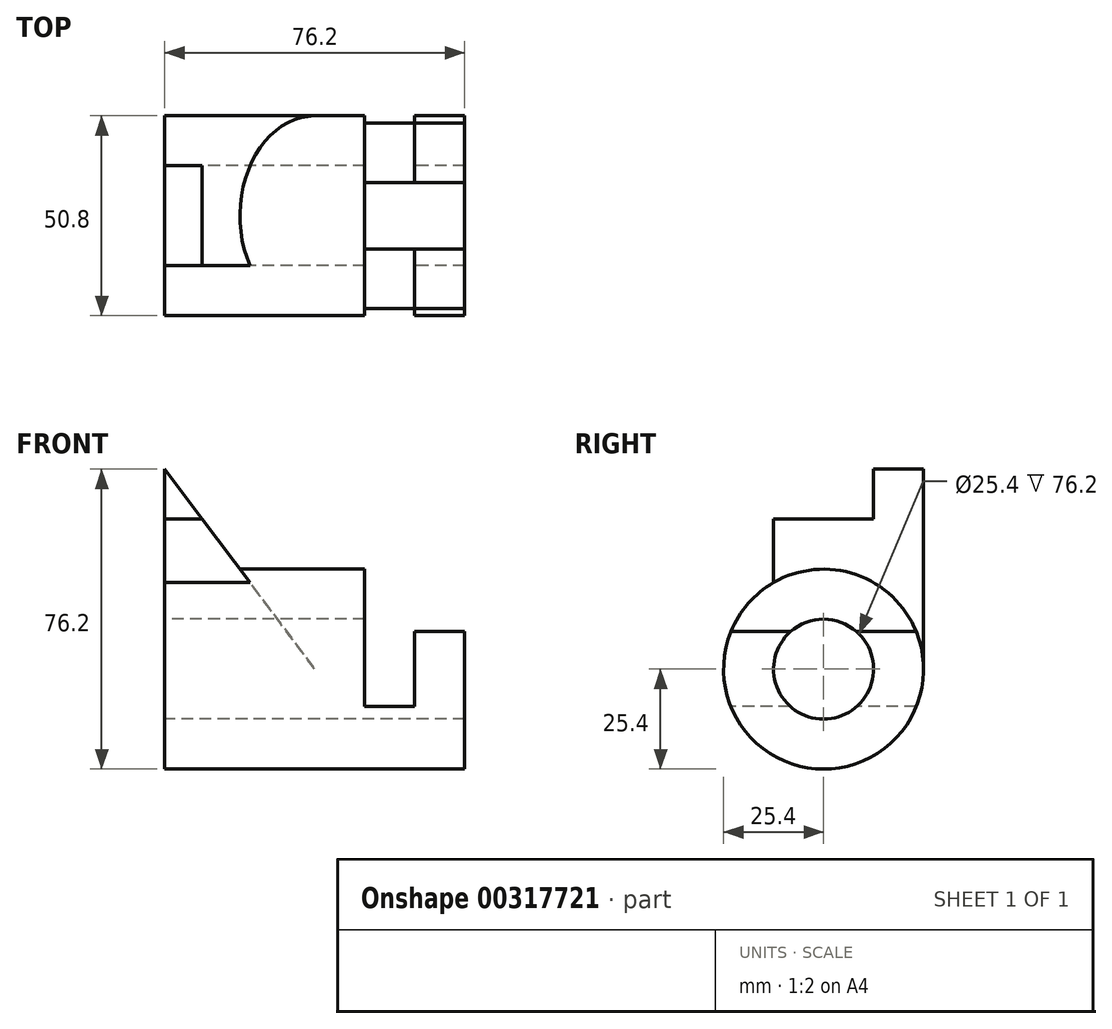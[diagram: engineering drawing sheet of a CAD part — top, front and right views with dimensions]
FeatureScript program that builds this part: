
annotation { "Feature Type Name" : "Feature", "Feature Type Description" : "" }
export const myFeature = defineFeature(function(context is Context, id is Id, definition is map)
    precondition{}
    {
        {
            var Q0;
            Q0=qCreatedBy(makeId("Right.planeOp"),FACE);
            var sketch = newSketch(context, id + "F0", { "sketchPlane" : qUnion([Q0])});
            skCircle(sketch, "E0", {"center": v(0, 0) * mm, "radius": 12.7 * mm});
            skCircle(sketch, "E1", {"center": v(0, 0) * mm, "radius": 25.4 * mm});
            skSolve(sketch);
        }
        {
            var Q0;
            Q0=makeQuery(id+"F0.imprint","IMPRINT",FACE,{"disambiguationData":[TD([[makeQuery(id+"F0.imprint","IMPRINT",EDGE,{"derivedFrom":sQuery(id+"F0.wireOp",EDGE,"E0")}),-1.0]])]});
            extrude(context, id + "F1", {"entities" : qUnion([Q0]), "depth" : 76.2 * mm});
        }
        {
            var Q0;
            Q0=qCreatedBy(makeId("Front.planeOp"),FACE);
            var sketch = newSketch(context, id + "F2", { "sketchPlane" : qUnion([Q0])});
            skLineSegment(sketch, "E2", {"start": v(50.8, 25.4) * mm, "end": v(50.8, -9.53) * mm});
            skLineSegment(sketch, "E3", {"start": v(50.8, -9.53) * mm, "end": v(63.5, -9.53) * mm});
            skLineSegment(sketch, "E4", {"start": v(63.5, -9.53) * mm, "end": v(63.5, 9.52) * mm});
            skLineSegment(sketch, "E5", {"start": v(63.5, 9.53) * mm, "end": v(76.2, 9.53) * mm});
            skLineSegment(sketch, "E6", {"start": v(76.2, 9.53) * mm, "end": v(76.2, 25.4) * mm});
            skLineSegment(sketch, "E7", {"start": v(76.2, 25.4) * mm, "end": v(50.8, 25.4) * mm});
            skLineSegment(sketch, "E8", {"start": v(0, 25.4) * mm, "end": v(76.2, 25.4) * mm});
            skSolve(sketch);
        }
        {
            var Q0;
            Q0 = qSketchRegion(id + "F2", true);
            extrude(context, id + "F3", {"entities" : qUnion([Q0]), "operationType" : NewBodyOperationType.REMOVE, "endBound" : BoundingType.SYMMETRIC, "oppositeDirection" : true, "depth" : 53.34 * mm});
        }
        {
            var Q0;
            Q0=qCreatedBy(makeId("Front.planeOp"),FACE);
            var sketch = newSketch(context, id + "F4", { "sketchPlane" : qUnion([Q0])});
            skLineSegment(sketch, "E9", {"start": v(0, 0) * mm, "end": v(0, 50.8) * mm});
            skLineSegment(sketch, "E10", {"start": v(0, 50.8) * mm, "end": v(38.1, 0) * mm});
            skLineSegment(sketch, "E11", {"start": v(38.1, 0) * mm, "end": v(0, 0) * mm});
            skSolve(sketch);
        }
        {
            var Q0;
            Q0=makeQuery(id+"F4.imprint","IMPRINT",FACE,{"disambiguationData":[TD([[makeQuery(id+"F4.imprint","IMPRINT",EDGE,{"derivedFrom":sQuery(id+"F4.wireOp",EDGE,"E9")}),-1.0]])]});
            extrude(context, id + "F5", {"entities" : qUnion([Q0]), "operationType" : NewBodyOperationType.ADD, "depth" : 12.7 * mm, "hasSecondDirection" : true, "secondDirectionOppositeDirection" : true, "secondDirectionDepth" : 25.4 * mm});
        }
        {
            var Q0;
            Q0=makeQuery(id+"F5.boolean.opBoolean","MERGE",FACE,{"derivedFrom":[makeQuery(id+"F1.opExtrude","CAP_FACE",FACE,{"disambiguationData":[OSD([sQuery(id+"F0.wireOp",EDGE,"E0"),sQuery(id+"F0.wireOp",EDGE,"E1")])],"isStart":true}),makeQuery(id+"F5.opExtrude","SWEPT_FACE",FACE,{"disambiguationData":[OSD([sQuery(id+"F4.wireOp",EDGE,"E9")])]})]});
            var sketch = newSketch(context, id + "F6", { "sketchPlane" : qUnion([Q0])});
            skLineSegment(sketch, "E12", {"start": v(12.7, 50.8) * mm, "end": v(-12.7, 50.8) * mm});
            skLineSegment(sketch, "E13", {"start": v(-12.7, 50.8) * mm, "end": v(-12.7, 38.1) * mm});
            skLineSegment(sketch, "E14", {"start": v(-12.7, 38.1) * mm, "end": v(12.7, 38.1) * mm});
            skLineSegment(sketch, "E15", {"start": v(12.7, 38.1) * mm, "end": v(12.7, 50.8) * mm});
            skSolve(sketch);
        }
        {
            var Q0;
            Q0 = qSketchRegion(id + "F6", true);
            extrude(context, id + "F7", {"entities" : qUnion([Q0]), "operationType" : NewBodyOperationType.REMOVE, "endBound" : BoundingType.THROUGH_ALL, "oppositeDirection" : true, "depth" : 25.4 * mm});
        }
        {
            var Q0;
            Q0=makeQuery(id+"F5.boolean.opBoolean","MERGE",FACE,{"derivedFrom":[makeQuery(id+"F1.opExtrude","CAP_FACE",FACE,{"disambiguationData":[OSD([sQuery(id+"F0.wireOp",EDGE,"E0"),sQuery(id+"F0.wireOp",EDGE,"E1")])],"isStart":true}),makeQuery(id+"F5.opExtrude","SWEPT_FACE",FACE,{"disambiguationData":[OSD([sQuery(id+"F4.wireOp",EDGE,"E9")])]})]});
            var sketch = newSketch(context, id + "F8", { "sketchPlane" : qUnion([Q0])});
            skCircle(sketch, "E16", {"center": v(0, 0) * mm, "radius": 12.7 * mm});
            skSolve(sketch);
        }
        {
            var Q0;
            Q0 = qSketchRegion(id + "F8", true);
            extrude(context, id + "F9", {"entities" : qUnion([Q0]), "operationType" : NewBodyOperationType.REMOVE, "endBound" : BoundingType.THROUGH_ALL, "oppositeDirection" : true, "depth" : 25.4 * mm});
        }
    });
